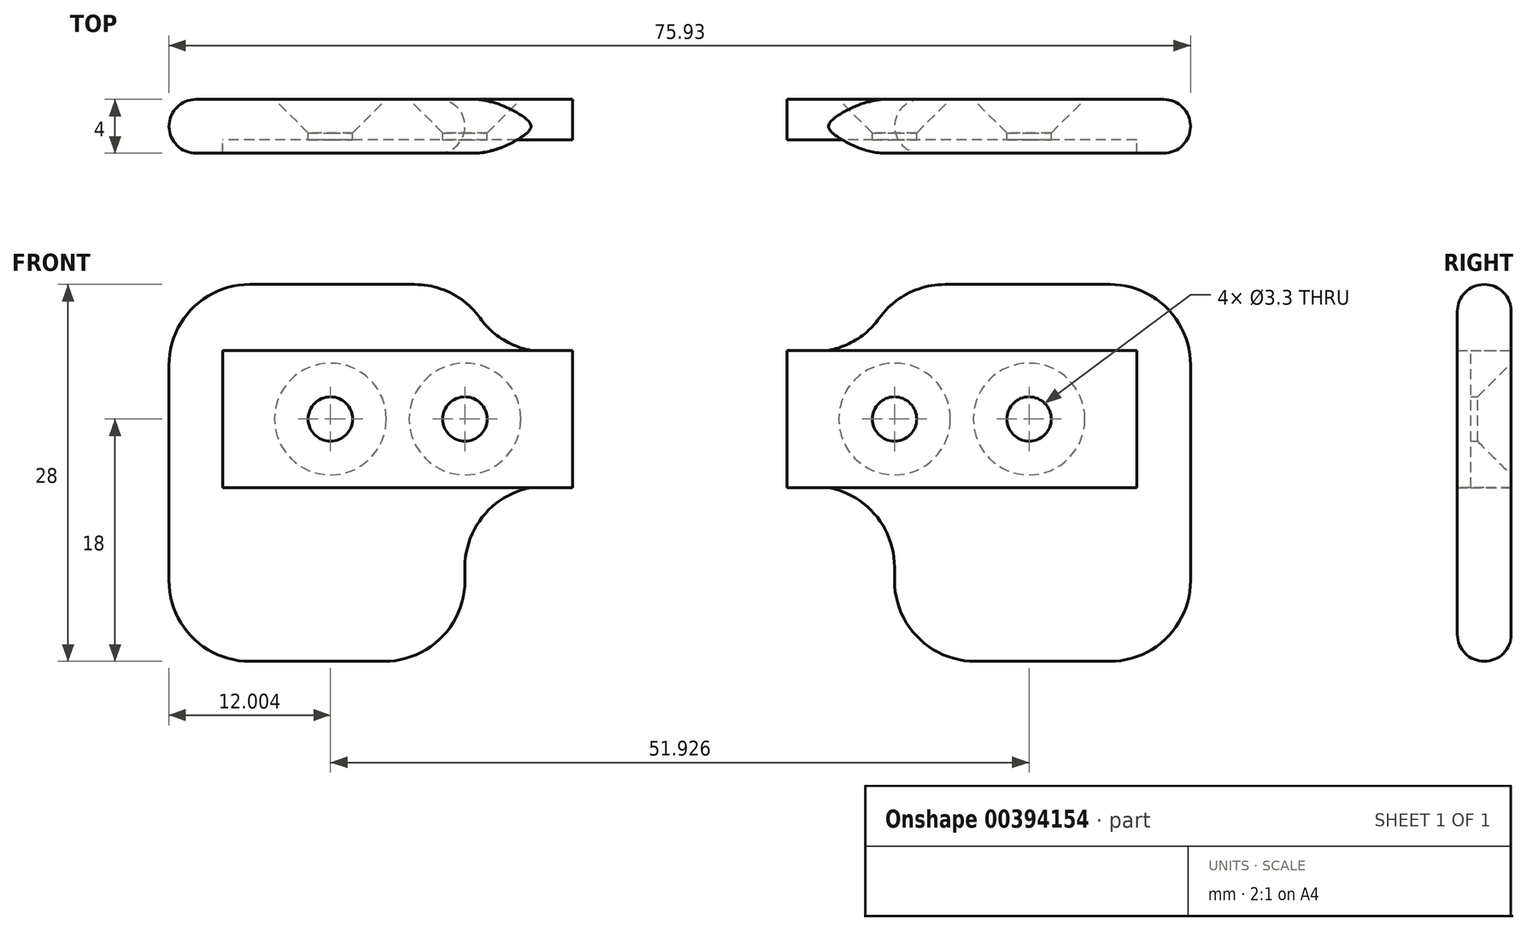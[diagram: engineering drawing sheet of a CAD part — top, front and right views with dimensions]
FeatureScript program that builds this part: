
annotation { "Feature Type Name" : "Feature", "Feature Type Description" : "" }
export const myFeature = defineFeature(function(context is Context, id is Id, definition is map)
    precondition{}
    {
        {
            var Q0;
            Q0=qCreatedBy(makeId("Front.planeOp"),FACE);
            var sketch = newSketch(context, id + "F0", { "sketchPlane" : qUnion([Q0])});
            skLineSegment(sketch, "E0.bottom", {"start": v(-15, 5) * mm, "end": v(-13, 5) * mm});
            skLineSegment(sketch, "E0.top", {"start": v(-15, -5) * mm, "end": v(-13, -5) * mm});
            skLineSegment(sketch, "E0.left", {"start": v(-15, 5) * mm, "end": v(-15, -5) * mm});
            skPoint(sketch, "E0.middle", {"position": v(0, 0) * mm});
            skCircle(sketch, "E1", {"center": v(-7, 0) * mm, "radius": 1.65 * mm});
            skCircle(sketch, "E2", {"center": v(3, 0) * mm, "radius": 1.65 * mm});
            skLineSegment(sketch, "E3.top", {"start": v(9, -18) * mm, "end": v(-1, -18) * mm});
            skLineSegment(sketch, "E3.left", {"start": v(15, -5) * mm, "end": v(15, -12) * mm});
            skLineSegment(sketch, "E3.right", {"start": v(-7, -11) * mm, "end": v(-7, -12) * mm});
            skLineSegment(sketch, "E4.top", {"start": v(9, 10) * mm, "end": v(-3.25, 10) * mm});
            skLineSegment(sketch, "E4.right", {"start": v(-7, 10) * mm, "end": v(-7, 11) * mm});
            skPoint(sketch, "E5.newPointA", {"position": v(15, 5) * mm});
            skArc(sketch, "E5.filletArc", {"start": v(-13, 5) * mm, "mid": v(-10.26, 5.66) * mm, "end": v(-8.13, 7.5) * mm});
            skArc(sketch, "E6.filletArc", {"start": v(-3.25, 10) * mm, "mid": v(-6, 9.34) * mm, "end": v(-8.13, 7.5) * mm});
            skLineSegment(sketch, "E7", {"start": v(15, 4) * mm, "end": v(15, -5) * mm});
            skPoint(sketch, "E8.visualSharp", {"position": v(15, 10) * mm});
            skArc(sketch, "E8.filletArc", {"start": v(15, 4) * mm, "mid": v(13.24, 8.24) * mm, "end": v(9, 10) * mm});
            skPoint(sketch, "E9.visualSharp", {"position": v(15, -18) * mm});
            skArc(sketch, "E9.filletArc", {"start": v(9, -18) * mm, "mid": v(13.24, -16.24) * mm, "end": v(15, -12) * mm});
            skPoint(sketch, "E10.visualSharp", {"position": v(-7, -18) * mm});
            skArc(sketch, "E10.filletArc", {"start": v(-7, -12) * mm, "mid": v(-5.24, -16.24) * mm, "end": v(-1, -18) * mm});
            skPoint(sketch, "E11.visualSharp", {"position": v(-7, -5) * mm});
            skArc(sketch, "E11.filletArc", {"start": v(-7, -11) * mm, "mid": v(-8.76, -6.76) * mm, "end": v(-13, -5) * mm});
            skLineSegment(sketch, "E12", {"start": v(-22.96, 0) * mm, "end": v(-22.96, 8.2) * mm});
            skLineSegment(sketch, "E13.MirrorCS", {"start": v(-30.93, 5) * mm, "end": v(-32.93, 5) * mm});
            skLineSegment(sketch, "E14.MirrorCS", {"start": v(-30.93, -5) * mm, "end": v(-32.93, -5) * mm});
            skLineSegment(sketch, "E15.MirrorCS", {"start": v(-38.93, -11) * mm, "end": v(-38.93, -12) * mm});
            skLineSegment(sketch, "E16.MirrorCS", {"start": v(-38.93, 10) * mm, "end": v(-38.93, 11) * mm});
            skArc(sketch, "E17.MirrorCS", {"start": v(-38.93, -11) * mm, "mid": v(-37.17, -6.76) * mm, "end": v(-32.93, -5) * mm});
            skPoint(sketch, "E18.MirrorP", {"position": v(-60.93, 5) * mm});
            skPoint(sketch, "E19.MirrorP", {"position": v(-38.93, -5) * mm});
            skCircle(sketch, "E20.MirrorC", {"center": v(-48.93, 0) * mm, "radius": 1.65 * mm});
            skPoint(sketch, "E21.MirrorP", {"position": v(-38.93, -18) * mm});
            skCircle(sketch, "E22.MirrorC", {"center": v(-38.93, 0) * mm, "radius": 1.65 * mm});
            skLineSegment(sketch, "E23.MirrorCS", {"start": v(-54.93, 10) * mm, "end": v(-42.67, 10) * mm});
            skArc(sketch, "E24.MirrorCS", {"start": v(-32.93, 5) * mm, "mid": v(-35.67, 5.66) * mm, "end": v(-37.8, 7.5) * mm});
            skArc(sketch, "E25.MirrorCS", {"start": v(-54.93, -18) * mm, "mid": v(-59.17, -16.24) * mm, "end": v(-60.93, -12) * mm});
            skArc(sketch, "E26.MirrorCS", {"start": v(-60.93, 4) * mm, "mid": v(-59.17, 8.24) * mm, "end": v(-54.93, 10) * mm});
            skArc(sketch, "E27.MirrorCS", {"start": v(-42.67, 10) * mm, "mid": v(-39.93, 9.34) * mm, "end": v(-37.8, 7.5) * mm});
            skArc(sketch, "E28.MirrorCS", {"start": v(-38.93, -12) * mm, "mid": v(-40.68, -16.24) * mm, "end": v(-44.93, -18) * mm});
            skPoint(sketch, "E29.MirrorP", {"position": v(-60.93, 10) * mm});
            skLineSegment(sketch, "E30.MirrorCS", {"start": v(-60.93, 4) * mm, "end": v(-60.93, -5) * mm});
            skPoint(sketch, "E31.MirrorP", {"position": v(-60.93, -18) * mm});
            skLineSegment(sketch, "E32.MirrorCS", {"start": v(-30.93, 5) * mm, "end": v(-30.93, -5) * mm});
            skLineSegment(sketch, "E33.MirrorCS", {"start": v(-54.93, -18) * mm, "end": v(-44.93, -18) * mm});
            skPoint(sketch, "E34.MirrorP", {"position": v(-45.93, 0) * mm});
            skLineSegment(sketch, "E35.MirrorCS", {"start": v(-60.93, -5) * mm, "end": v(-60.93, -12) * mm});
            skLineSegment(sketch, "E36.bottom", {"start": v(11, -5.1) * mm, "end": v(-15, -5.1) * mm});
            skLineSegment(sketch, "E36.top", {"start": v(11, 5.1) * mm, "end": v(-15, 5.1) * mm});
            skLineSegment(sketch, "E36.left", {"start": v(11, -5.1) * mm, "end": v(11, 5.1) * mm});
            skLineSegment(sketch, "E36.right", {"start": v(-15, -5.1) * mm, "end": v(-15, 5.1) * mm});
            skPoint(sketch, "E37.firstSnap0", {"position": v(-30.93, 0) * mm});
            skLineSegment(sketch, "E37.bottom", {"start": v(-30.93, -5.1) * mm, "end": v(-56.93, -5.1) * mm});
            skLineSegment(sketch, "E37.top", {"start": v(-30.93, 5.1) * mm, "end": v(-56.93, 5.1) * mm});
            skLineSegment(sketch, "E37.left", {"start": v(-30.93, -5.1) * mm, "end": v(-30.93, 5.1) * mm});
            skLineSegment(sketch, "E37.right", {"start": v(-56.93, -5.1) * mm, "end": v(-56.93, 5.1) * mm});
            skSolve(sketch);
        }
        {
            var Q0;
            Q0=makeQuery(id+"F0.imprint","IMPRINT",FACE,{"disambiguationData":[TD([[makeQuery(id+"F0.imprint","IMPRINT",EDGE,{"derivedFrom":sQuery(id+"F0.wireOp",EDGE,"E3.top")}),-1.0]])]});
            var Q1;
            {var subQ1=sQuery(id+"F0.wireOp",EDGE,"E15.MirrorCS");Q1=makeQuery(id+"F0.imprint","IMPRINT",FACE,{"disambiguationData":[TD([[makeQuery(id+"F0.imprint","IMPRINT",EDGE,{"derivedFrom":subQ1}),-1.0]])]});}
            extrude(context, id + "F1", {"entities" : qUnion([Q0, Q1]), "depth" : 4 * mm});
        }
        {
            var Q0;
            Q0 = qSketchRegion(id + "F0", true);
            extrude(context, id + "F2", {"entities" : qUnion([Q0]), "operationType" : NewBodyOperationType.ADD, "depth" : 3 * mm});
        }
        {
            var Q0;
            Q0=makeQuery(id+"F1.opExtrude","CAP_EDGE",EDGE,{"disambiguationData":[OSD([sQuery(id+"F0.wireOp",EDGE,"E26.MirrorCS")])],"isStart":false});
            var Q1;
            Q1=makeQuery(id+"F1.opExtrude","CAP_EDGE",EDGE,{"disambiguationData":[OSD([sQuery(id+"F0.wireOp",EDGE,"E4.top")])],"isStart":false});
            var Q2;
            Q2=makeQuery(id+"F1.opExtrude","CAP_EDGE",EDGE,{"disambiguationData":[OSD([sQuery(id+"F0.wireOp",EDGE,"E28.MirrorCS")])],"isStart":true});
            var Q3;
            Q3=makeQuery(id+"F1.opExtrude","CAP_EDGE",EDGE,{"disambiguationData":[OSD([sQuery(id+"F0.wireOp",EDGE,"E9.filletArc")])],"isStart":true});
            fillet(context, id + "F3", {"entities" : qUnion([Q0, Q1, Q2, Q3]), "radius" : 2 * mm, "tangentPropagation" : true, "allowEdgeOverflow" : false});
        }
        {
            var Q0;
            Q0=makeQuery(id+"F2.opExtrude","CAP_EDGE",EDGE,{"disambiguationData":[OSD([sQuery(id+"F0.wireOp",EDGE,"E2")])],"isStart":true});
            var Q1;
            Q1=makeQuery(id+"F2.opExtrude","CAP_EDGE",EDGE,{"disambiguationData":[OSD([sQuery(id+"F0.wireOp",EDGE,"E1")])],"isStart":true});
            var Q2;
            Q2=makeQuery(id+"F2.opExtrude","CAP_EDGE",EDGE,{"disambiguationData":[OSD([sQuery(id+"F0.wireOp",EDGE,"E22.MirrorC")])],"isStart":true});
            var Q3;
            Q3=makeQuery(id+"F2.opExtrude","CAP_EDGE",EDGE,{"disambiguationData":[OSD([sQuery(id+"F0.wireOp",EDGE,"E20.MirrorC")])],"isStart":true});
            chamfer(context, id + "F4", {"entities" : qUnion([Q0, Q1, Q2, Q3]), "width" : 2.5 * mm, "tangentPropagation" : true});
        }
    });
